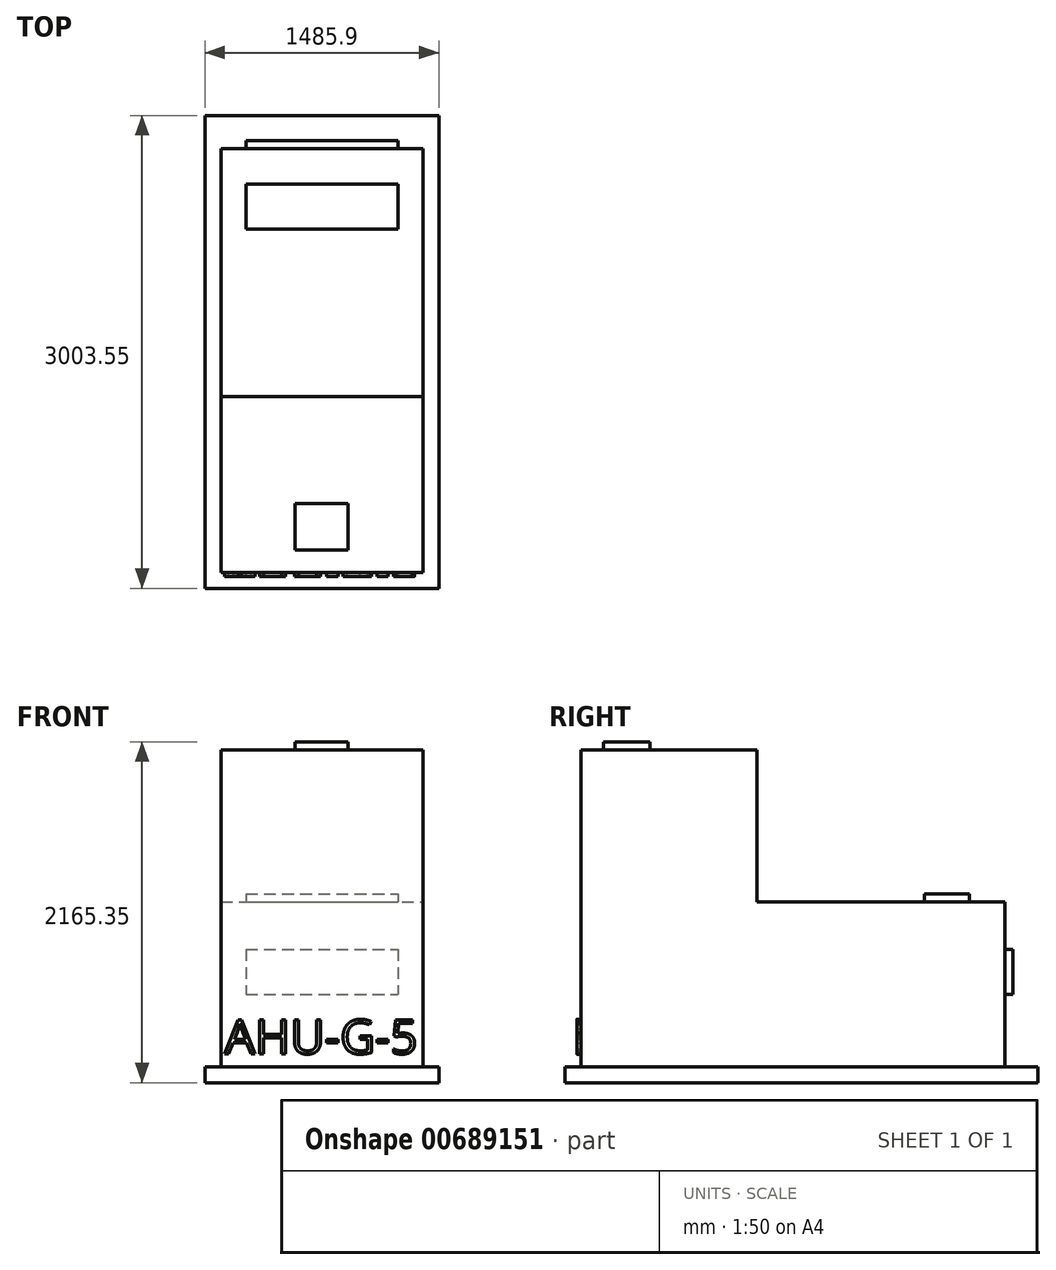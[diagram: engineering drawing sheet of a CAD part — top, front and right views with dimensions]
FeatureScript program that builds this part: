
annotation { "Feature Type Name" : "Feature", "Feature Type Description" : "" }
export const myFeature = defineFeature(function(context is Context, id is Id, definition is map)
    precondition{}
    {
        {
            var Q0;
            Q0=qCreatedBy(makeId("Front.planeOp"),FACE);
            var sketch = newSketch(context, id + "F0", { "sketchPlane" : qUnion([Q0])});
            skLineSegment(sketch, "E0.bottom", {"start": v(-639.94, 495.31) * mm, "end": v(642.76, 495.31) * mm});
            skLineSegment(sketch, "E0.top", {"start": v(-639.94, -552.44) * mm, "end": v(642.76, -552.44) * mm});
            skLineSegment(sketch, "E0.left", {"start": v(-639.94, 495.31) * mm, "end": v(-639.94, -552.44) * mm});
            skLineSegment(sketch, "E0.right", {"start": v(642.76, 495.31) * mm, "end": v(642.76, -552.44) * mm});
            skSolve(sketch);
        }
        {
            var Q0;
            Q0=qSketchRegion(id+"F0",true);
            extrude(context, id + "F1", {"entities" : qUnion([Q0]), "depth" : 2692.4 * mm, "offsetDistance" : 25.4 * mm});
        }
        {
            var Q0;
            Q0=makeQuery(id+"F1.opExtrude","CAP_FACE",FACE,{"disambiguationData":[OSD([sQuery(id+"F0.wireOp",EDGE,"E0.bottom"),sQuery(id+"F0.wireOp",EDGE,"E0.top"),sQuery(id+"F0.wireOp",EDGE,"E0.left"),sQuery(id+"F0.wireOp",EDGE,"E0.right")])],"isStart":false});
            var sketch = newSketch(context, id + "F2", { "sketchPlane" : qUnion([Q0])});
            skLineSegment(sketch, "E1.bottom", {"start": v(-741.54, -552.44) * mm, "end": v(744.36, -552.44) * mm});
            skLineSegment(sketch, "E1.top", {"start": v(-741.54, -654.04) * mm, "end": v(744.36, -654.04) * mm});
            skLineSegment(sketch, "E1.left", {"start": v(-741.54, -552.44) * mm, "end": v(-741.54, -654.04) * mm});
            skLineSegment(sketch, "E1.right", {"start": v(744.36, -552.44) * mm, "end": v(744.36, -654.04) * mm});
            skSolve(sketch);
        }
        {
            var Q0;
            Q0=qSketchRegion(id+"F2",true);
            extrude(context, id + "F3", {"entities" : qUnion([Q0]), "depth" : 101.6 * mm, "offsetDistance" : 25.4 * mm});
        }
        {
            var Q0;
            Q0=makeQuery(id+"F3.opExtrude","CAP_FACE",FACE,{"disambiguationData":[OSD([sQuery(id+"F2.wireOp",EDGE,"E1.bottom"),sQuery(id+"F2.wireOp",EDGE,"E1.top"),sQuery(id+"F2.wireOp",EDGE,"E1.left"),sQuery(id+"F2.wireOp",EDGE,"E1.right")])],"isStart":true});
            extrude(context, id + "F4", {"entities" : qUnion([Q0]), "operationType" : NewBodyOperationType.ADD, "depth" : 2901.95 * mm, "offsetDistance" : 25.4 * mm});
        }
        {
            var Q0;
            Q0=makeQuery(id+"F1.opExtrude","CAP_FACE",FACE,{"disambiguationData":[OSD([sQuery(id+"F0.wireOp",EDGE,"E0.bottom"),sQuery(id+"F0.wireOp",EDGE,"E0.top"),sQuery(id+"F0.wireOp",EDGE,"E0.left"),sQuery(id+"F0.wireOp",EDGE,"E0.right")])],"isStart":false});
            var sketch = newSketch(context, id + "F5", { "sketchPlane" : qUnion([Q0])});
            skText(sketch, "E2", { "text": "AHU-G-5", "fontName": "OpenSans-Regular.ttf"});
            const initialGuessF5  = {"E2": [-0.61556, -0.47083, 1, 0, 0.21805]};
            skSetInitialGuess(sketch, initialGuessF5);
            skSolve(sketch);
        }
        {
            var Q0;
            Q0=qSketchRegion(id+"F5",true);
            extrude(context, id + "F6", {"entities" : qUnion([Q0]), "operationType" : NewBodyOperationType.ADD, "depth" : 25.4 * mm, "offsetDistance" : 25.4 * mm});
        }
        {
            var Q0;
            Q0=makeQuery(id+"F1.opExtrude","SWEPT_FACE",FACE,{"disambiguationData":[OSD([sQuery(id+"F0.wireOp",EDGE,"E0.bottom")])]});
            var sketch = newSketch(context, id + "F7", { "sketchPlane" : qUnion([Q0])});
            skLineSegment(sketch, "E3.bottom", {"start": v(-481.2, -511.17) * mm, "end": v(484, -511.17) * mm});
            skLineSegment(sketch, "E3.top", {"start": v(-481.2, -225.43) * mm, "end": v(484, -225.42) * mm});
            skLineSegment(sketch, "E3.left", {"start": v(-481.2, -511.17) * mm, "end": v(-481.2, -225.43) * mm});
            skLineSegment(sketch, "E3.right", {"start": v(484, -511.17) * mm, "end": v(484, -225.42) * mm});
            skSolve(sketch);
        }
        {
            var Q0;
            Q0=qSketchRegion(id+"F7",true);
            extrude(context, id + "F8", {"entities" : qUnion([Q0]), "operationType" : NewBodyOperationType.ADD, "depth" : 50.8 * mm, "offsetDistance" : 25.4 * mm});
        }
        {
            var Q0;
            Q0=makeQuery(id+"F1.opExtrude","CAP_FACE",FACE,{"disambiguationData":[OSD([sQuery(id+"F0.wireOp",EDGE,"E0.bottom"),sQuery(id+"F0.wireOp",EDGE,"E0.top"),sQuery(id+"F0.wireOp",EDGE,"E0.left"),sQuery(id+"F0.wireOp",EDGE,"E0.right")])],"isStart":true});
            var sketch = newSketch(context, id + "F9", { "sketchPlane" : qUnion([Q0])});
            skLineSegment(sketch, "E4.bottom", {"start": v(481.2, 193.69) * mm, "end": v(-484, 193.69) * mm});
            skLineSegment(sketch, "E4.top", {"start": v(481.2, -92.06) * mm, "end": v(-484, -92.06) * mm});
            skLineSegment(sketch, "E4.left", {"start": v(481.2, 193.69) * mm, "end": v(481.2, -92.06) * mm});
            skLineSegment(sketch, "E4.right", {"start": v(-484, 193.69) * mm, "end": v(-484, -92.06) * mm});
            skSolve(sketch);
        }
        {
            var Q0;
            Q0=qSketchRegion(id+"F9",true);
            extrude(context, id + "F10", {"entities" : qUnion([Q0]), "operationType" : NewBodyOperationType.ADD, "depth" : 50.8 * mm, "offsetDistance" : 25.4 * mm});
        }
        {
            var Q0;
            Q0=makeQuery(id+"F1.opExtrude","SWEPT_FACE",FACE,{"disambiguationData":[OSD([sQuery(id+"F0.wireOp",EDGE,"E0.bottom")])]});
            var sketch = newSketch(context, id + "F11", { "sketchPlane" : qUnion([Q0])});
            skLineSegment(sketch, "E5.bottom", {"start": v(-639.94, -1574.8) * mm, "end": v(642.76, -1574.8) * mm});
            skLineSegment(sketch, "E5.top", {"start": v(-639.94, -2692.4) * mm, "end": v(642.76, -2692.4) * mm});
            skLineSegment(sketch, "E5.left", {"start": v(-639.94, -1574.8) * mm, "end": v(-639.94, -2692.4) * mm});
            skLineSegment(sketch, "E5.right", {"start": v(642.76, -1574.8) * mm, "end": v(642.76, -2692.4) * mm});
            skSolve(sketch);
        }
        {
            var Q0;
            Q0 = qSketchRegion(id + "F11", true);
            extrude(context, id + "F12", {"entities" : qUnion([Q0]), "operationType" : NewBodyOperationType.ADD, "depth" : 965.2 * mm, "offsetDistance" : 25.4 * mm});
        }
        {
            var Q0;
            Q0=makeQuery(id+"F12.opExtrude","CAP_FACE",FACE,{"disambiguationData":[OSD([sQuery(id+"F11.wireOp",EDGE,"E5.bottom"),sQuery(id+"F11.wireOp",EDGE,"E5.top"),sQuery(id+"F11.wireOp",EDGE,"E5.left"),sQuery(id+"F11.wireOp",EDGE,"E5.right")])],"isStart":false});
            var sketch = newSketch(context, id + "F13", { "sketchPlane" : qUnion([Q0])});
            skLineSegment(sketch, "E6.bottom", {"start": v(-170.04, -2254.25) * mm, "end": v(166.5, -2254.25) * mm});
            skLineSegment(sketch, "E6.top", {"start": v(-170.04, -2549.53) * mm, "end": v(166.5, -2549.53) * mm});
            skLineSegment(sketch, "E6.left", {"start": v(-170.04, -2254.25) * mm, "end": v(-170.04, -2549.53) * mm});
            skLineSegment(sketch, "E6.right", {"start": v(166.5, -2254.25) * mm, "end": v(166.5, -2549.53) * mm});
            skSolve(sketch);
        }
        {
            var Q0;
            Q0 = qSketchRegion(id + "F13", true);
            extrude(context, id + "F14", {"entities" : qUnion([Q0]), "operationType" : NewBodyOperationType.ADD, "depth" : 50.8 * mm, "offsetDistance" : 25.4 * mm});
        }
    });
